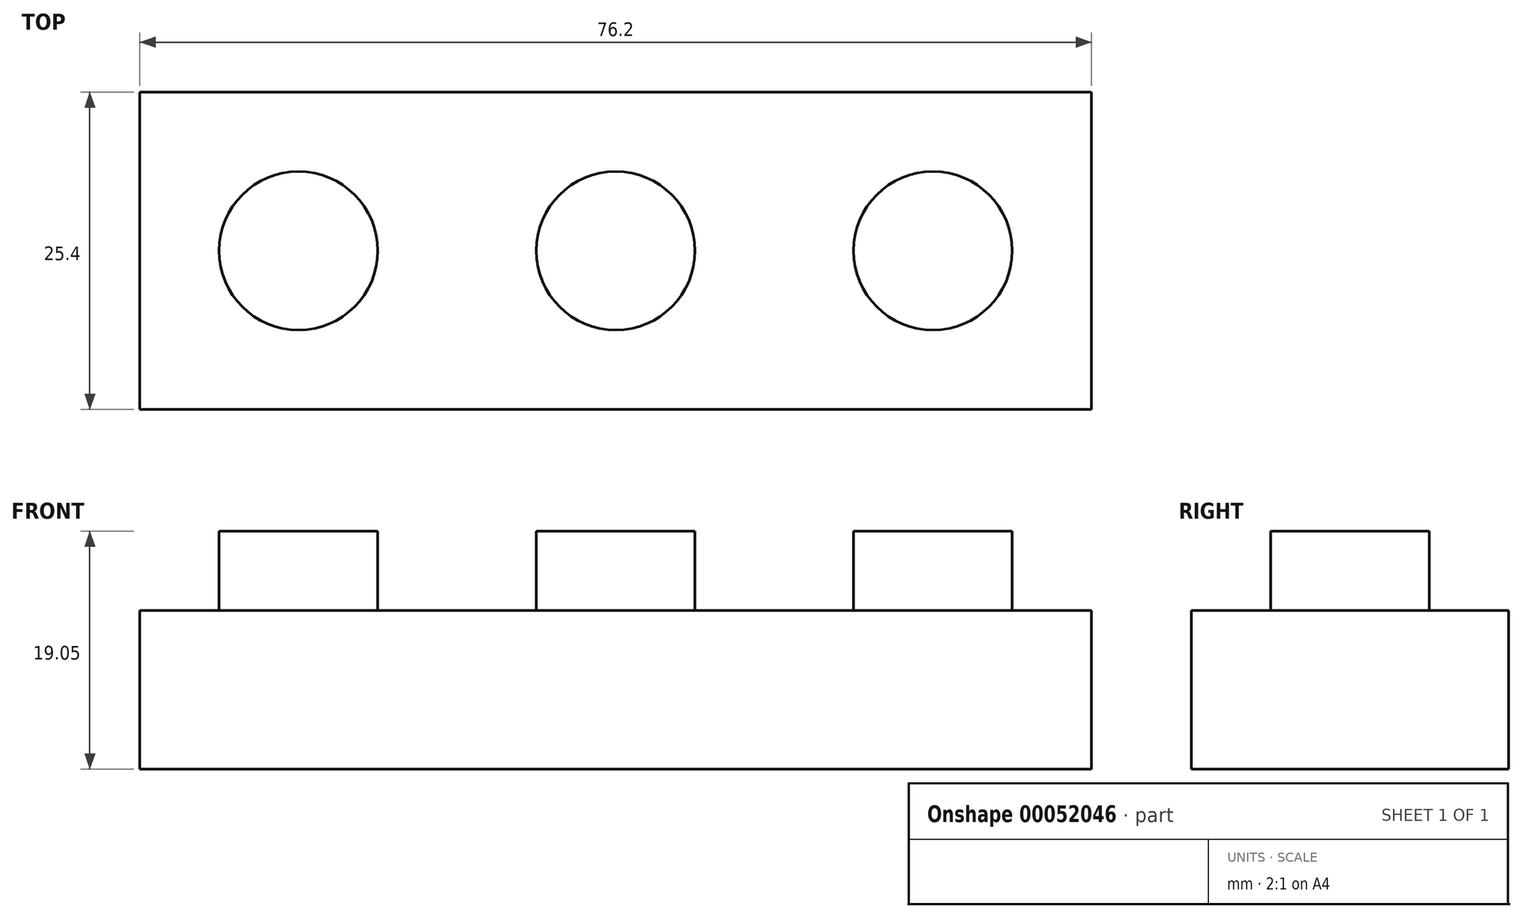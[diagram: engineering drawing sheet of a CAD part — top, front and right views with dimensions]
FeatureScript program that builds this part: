
annotation { "Feature Type Name" : "Feature", "Feature Type Description" : "" }
export const myFeature = defineFeature(function(context is Context, id is Id, definition is map)
    precondition{}
    {
        {
            var Q0;
            Q0=qCreatedBy(makeId("Top.planeOp"),FACE);
            var sketch = newSketch(context, id + "F0", { "sketchPlane" : qUnion([Q0])});
            skLineSegment(sketch, "E0.bottom", {"start": v(0, 0) * mm, "end": v(76.2, 0) * mm});
            skLineSegment(sketch, "E0.top", {"start": v(0, 25.4) * mm, "end": v(76.2, 25.4) * mm});
            skLineSegment(sketch, "E0.left", {"start": v(0, 0) * mm, "end": v(0, 25.4) * mm});
            skLineSegment(sketch, "E0.right", {"start": v(76.2, 0) * mm, "end": v(76.2, 25.4) * mm});
            skSolve(sketch);
        }
        {
            var Q0;
            Q0=makeQuery(id+"F0.imprint","IMPRINT",FACE,{"disambiguationData":[TD([[makeQuery(id+"F0.imprint","IMPRINT",EDGE,{"derivedFrom":sQuery(id+"F0.wireOp",EDGE,"E0.bottom")}),1.0]])]});
            extrude(context, id + "F1", {"entities" : qUnion([Q0]), "depth" : 12.7 * mm});
        }
        {
            var Q0;
            Q0=makeQuery(id+"F1.opExtrude","CAP_FACE",FACE,{"disambiguationData":[OSD([sQuery(id+"F0.wireOp",EDGE,"E0.bottom"),sQuery(id+"F0.wireOp",EDGE,"E0.top"),sQuery(id+"F0.wireOp",EDGE,"E0.left"),sQuery(id+"F0.wireOp",EDGE,"E0.right")])],"isStart":false});
            var sketch = newSketch(context, id + "F2", { "sketchPlane" : qUnion([Q0])});
            skPoint(sketch, "E1", {"position": v(12.7, 12.7) * mm});
            skPoint(sketch, "E2", {"position": v(38.1, 12.7) * mm});
            skPoint(sketch, "E3", {"position": v(63.5, 12.7) * mm});
            skCircle(sketch, "E4", {"center": v(12.7, 12.7) * mm, "radius": 6.35 * mm});
            skCircle(sketch, "E5", {"center": v(38.1, 12.7) * mm, "radius": 6.35 * mm});
            skCircle(sketch, "E6", {"center": v(63.5, 12.7) * mm, "radius": 6.35 * mm});
            skSolve(sketch);
        }
        {
            var Q0;
            Q0=makeQuery(id+"F2.imprint","IMPRINT",FACE,{"disambiguationData":[TD([[makeQuery(id+"F2.imprint","IMPRINT",EDGE,{"derivedFrom":sQuery(id+"F2.wireOp",EDGE,"E4")}),1.0]])]});
            var Q1;
            Q1=makeQuery(id+"F2.imprint","IMPRINT",FACE,{"disambiguationData":[TD([[makeQuery(id+"F2.imprint","IMPRINT",EDGE,{"derivedFrom":sQuery(id+"F2.wireOp",EDGE,"E5")}),1.0]])]});
            var Q2;
            Q2=makeQuery(id+"F2.imprint","IMPRINT",FACE,{"disambiguationData":[TD([[makeQuery(id+"F2.imprint","IMPRINT",EDGE,{"derivedFrom":sQuery(id+"F2.wireOp",EDGE,"E6")}),1.0]])]});
            extrude(context, id + "F3", {"entities" : qUnion([Q0, Q1, Q2]), "operationType" : NewBodyOperationType.ADD, "depth" : 6.35 * mm});
        }
    });
